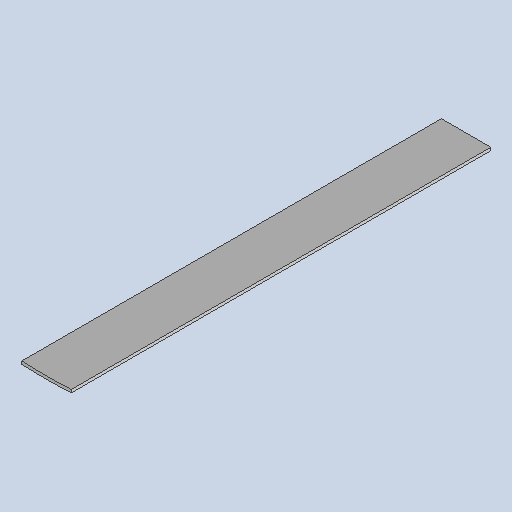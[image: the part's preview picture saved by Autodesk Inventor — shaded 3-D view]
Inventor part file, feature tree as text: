
AUTODESK INVENTOR PART (.ipt)
format: ipt  version: 2025 (Build 290162010, 162A)  size: 113,664 bytes
history: native  units: mm
features: other x3, sheet_metal_op x1, sketch x1
ambient origin geometry x8: Origin, YZ Plane, XZ Plane, XY Plane, X Axis, Y Axis, Z Axis, Center Point
bodies: Body1 (feature_tree)
feature tree (5):
  other  "BSH 504 inner cross"
  sheet_metal_op  "Face2"
  sketch  "Sketch1"  dims[d11=1100.0mm d12=900.0mm d13=25.0mm d14=25.0mm d15=3.0mm d16=25.0mm]
  other  "Plate2"
  other  "Definition1"
